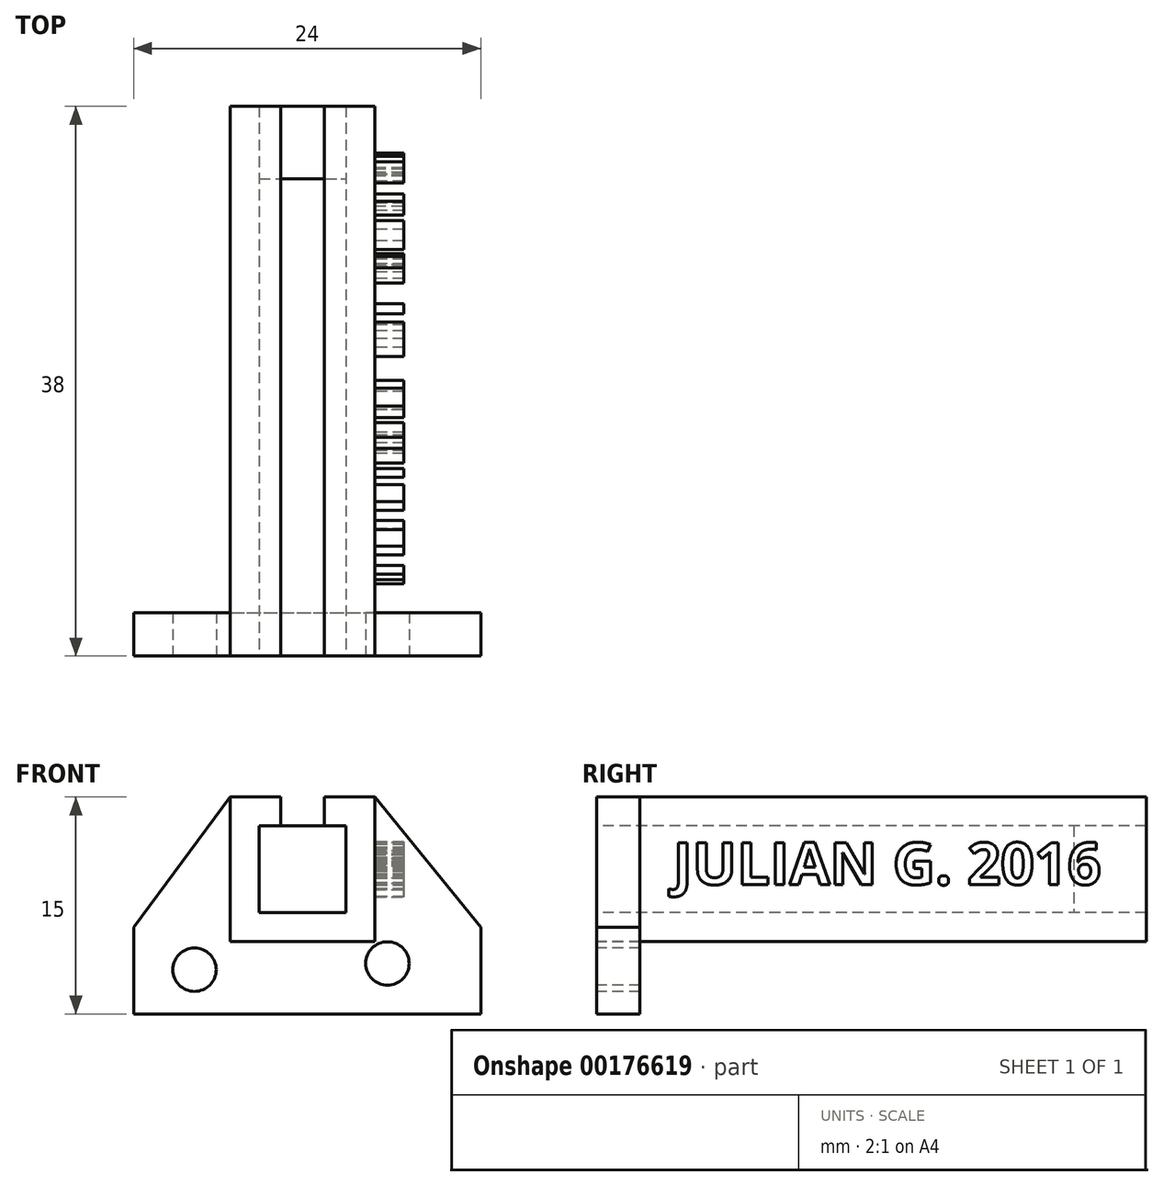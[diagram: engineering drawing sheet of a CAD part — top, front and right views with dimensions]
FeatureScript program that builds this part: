
annotation { "Feature Type Name" : "Feature", "Feature Type Description" : "" }
export const myFeature = defineFeature(function(context is Context, id is Id, definition is map)
    precondition{}
    {
        {
            var Q0;
            Q0=qCreatedBy(makeId("Front.planeOp"),FACE);
            var sketch = newSketch(context, id + "F0", { "sketchPlane" : qUnion([Q0])});
            skLineSegment(sketch, "E0", {"start": v(6.68, 0) * mm, "end": v(0, -9) * mm});
            skLineSegment(sketch, "E1", {"start": v(0, -9) * mm, "end": v(0, -15) * mm});
            skLineSegment(sketch, "E2", {"start": v(0, -15) * mm, "end": v(24, -15) * mm});
            skLineSegment(sketch, "E3", {"start": v(24, -15) * mm, "end": v(24, -9) * mm});
            skLineSegment(sketch, "E4", {"start": v(24, -9) * mm, "end": v(16.68, 0) * mm});
            skLineSegment(sketch, "E5", {"start": v(16.68, 0) * mm, "end": v(6.68, 0) * mm});
            skLineSegment(sketch, "E6.bottom", {"start": v(8.68, -2) * mm, "end": v(14.68, -2) * mm});
            skLineSegment(sketch, "E6.top", {"start": v(8.68, -8) * mm, "end": v(14.68, -8) * mm});
            skLineSegment(sketch, "E6.left", {"start": v(8.68, -2) * mm, "end": v(8.68, -8) * mm});
            skLineSegment(sketch, "E6.right", {"start": v(14.68, -2) * mm, "end": v(14.68, -8) * mm});
            skLineSegment(sketch, "E7.bottom", {"start": v(6.68, 0) * mm, "end": v(16.68, 0) * mm});
            skLineSegment(sketch, "E7.top", {"start": v(6.68, -10) * mm, "end": v(16.68, -10) * mm});
            skLineSegment(sketch, "E7.left", {"start": v(6.68, 0) * mm, "end": v(6.68, -10) * mm});
            skLineSegment(sketch, "E7.right", {"start": v(16.68, 0) * mm, "end": v(16.68, -10) * mm});
            skLineSegment(sketch, "E8.bottom", {"start": v(10.18, 0) * mm, "end": v(13.18, 0) * mm});
            skLineSegment(sketch, "E8.top", {"start": v(10.18, -2) * mm, "end": v(13.18, -2) * mm});
            skLineSegment(sketch, "E8.left", {"start": v(10.18, 0) * mm, "end": v(10.18, -2) * mm});
            skLineSegment(sketch, "E8.right", {"start": v(13.18, 0) * mm, "end": v(13.18, -2) * mm});
            skCircle(sketch, "E9", {"center": v(4.2, -11.94) * mm, "radius": 1.5 * mm});
            skCircle(sketch, "E10", {"center": v(17.55, -11.51) * mm, "radius": 1.5 * mm});
            skSolve(sketch);
        }
        {
            var Q0;
            Q0=makeQuery(id+"F0.imprint","IMPRINT",FACE,{"disambiguationData":[TD([[makeQuery(id+"F0.imprint","IMPRINT",EDGE,{"derivedFrom":sQuery(id+"F0.wireOp",EDGE,"E6.top")}),-1.0]])]});
            extrude(context, id + "F1", {"entities" : qUnion([Q0]), "oppositeDirection" : true, "depth" : 38 * mm});
        }
        {
            var Q0;
            Q0=makeQuery(id+"F0.imprint","IMPRINT",FACE,{"disambiguationData":[TD([[makeQuery(id+"F0.imprint","IMPRINT",EDGE,{"derivedFrom":sQuery(id+"F0.wireOp",EDGE,"E0")}),1.0]])]});
            extrude(context, id + "F2", {"entities" : qUnion([Q0]), "oppositeDirection" : true, "depth" : 3 * mm});
        }
        {
            var Q0;
            Q0=makeQuery(id+"F0.imprint","IMPRINT",FACE,{"disambiguationData":[TD([[makeQuery(id+"F0.imprint","IMPRINT",EDGE,{"derivedFrom":sQuery(id+"F0.wireOp",EDGE,"E6.top")}),1.0]])]});
            var Q1;
            Q1=makeQuery(id+"F0.imprint","IMPRINT",FACE,{"disambiguationData":[TD([[makeQuery(id+"F0.imprint","IMPRINT",EDGE,{"derivedFrom":sQuery(id+"F0.wireOp",EDGE,"E8.bottom")}),-1.0]])]});
            extrude(context, id + "F3", {"entities" : qUnion([Q0, Q1]), "oppositeDirection" : true, "depth" : 38 * mm});
        }
        {
            var Q0;
            Q0=makeQuery(id+"F0.imprint","IMPRINT",FACE,{"disambiguationData":[TD([[makeQuery(id+"F0.imprint","IMPRINT",EDGE,{"derivedFrom":sQuery(id+"F0.wireOp",EDGE,"E6.top")}),1.0]])]});
            var Q1;
            Q1=makeQuery(id+"F0.imprint","IMPRINT",FACE,{"disambiguationData":[TD([[makeQuery(id+"F0.imprint","IMPRINT",EDGE,{"derivedFrom":sQuery(id+"F0.wireOp",EDGE,"E8.bottom")}),-1.0]])]});
            extrude(context, id + "F4", {"entities" : qUnion([Q0, Q1]), "operationType" : NewBodyOperationType.REMOVE, "oppositeDirection" : true, "depth" : 33 * mm});
        }
        {
            var Q0;
            Q0=makeQuery(id+"F1.opExtrude","SWEPT_FACE",FACE,{"disambiguationData":[OSD([sQuery(id+"F0.wireOp",EDGE,"E7.right")])]});
            var sketch = newSketch(context, id + "F5", { "sketchPlane" : qUnion([Q0])});
            skText(sketch, "E11", { "text": "JULIAN G. 2016", "fontName": "OpenSans-Bold.ttf"});
            const initialGuessF5  = {"E11": [0.00529, -0.00606, 1, 0, 0.00292]};
            skSetInitialGuess(sketch, initialGuessF5);
            skSolve(sketch);
        }
        {
            var Q0;
            Q0 = qSketchRegion(id + "F5", true);
            extrude(context, id + "F6", {"entities" : qUnion([Q0]), "operationType" : NewBodyOperationType.ADD, "depth" : 2 * mm});
        }
    });
